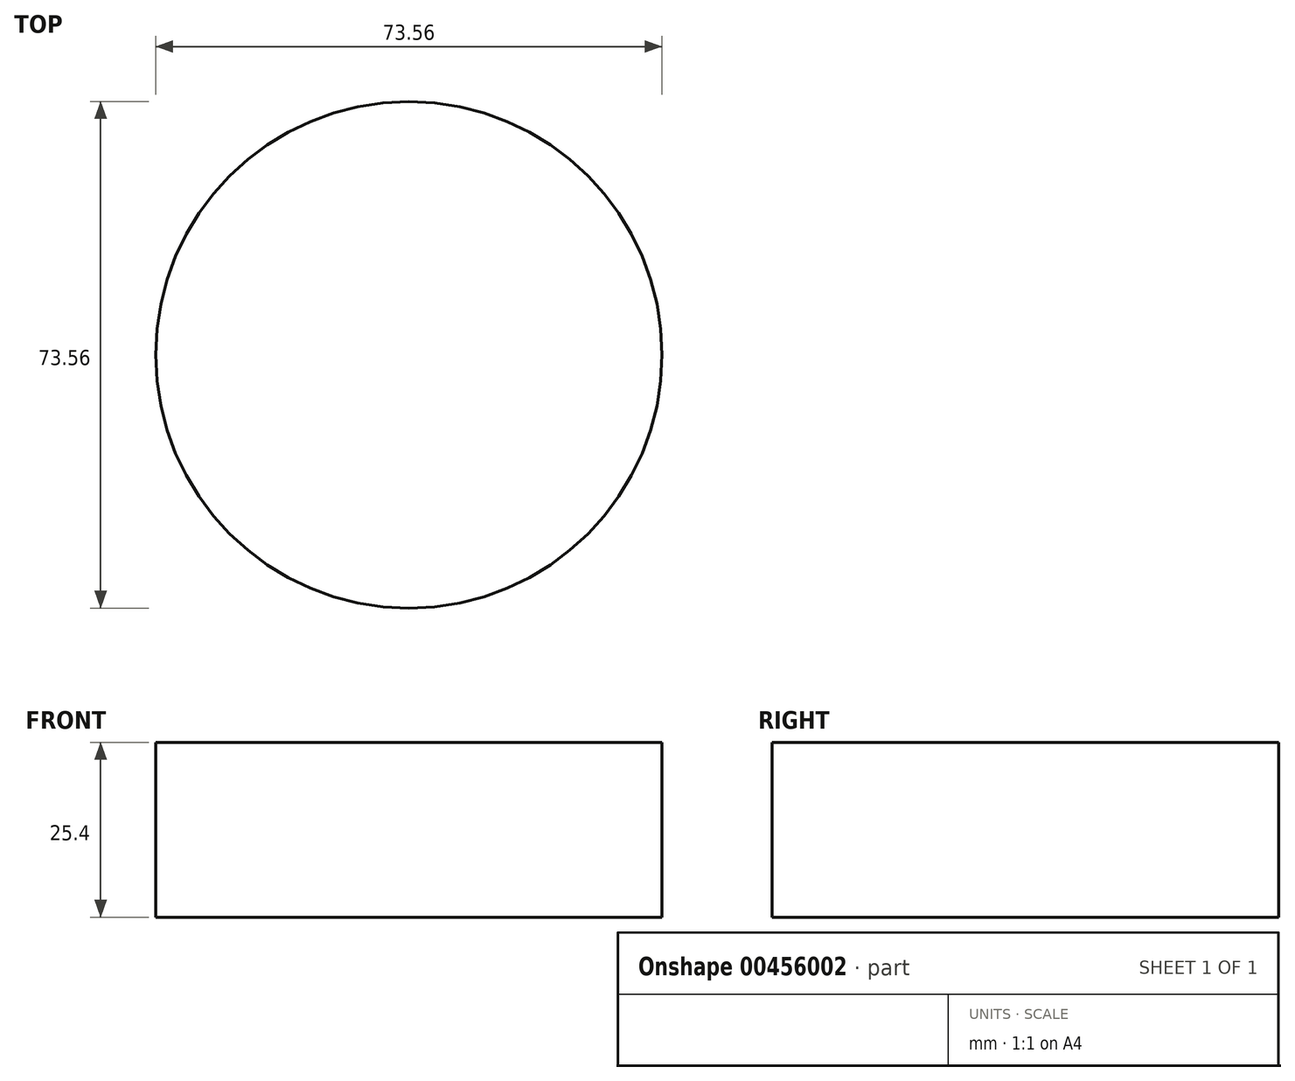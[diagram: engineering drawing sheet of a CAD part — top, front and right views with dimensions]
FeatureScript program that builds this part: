
annotation { "Feature Type Name" : "Feature", "Feature Type Description" : "" }
export const myFeature = defineFeature(function(context is Context, id is Id, definition is map)
    precondition{}
    {
        {
            var Q0;
            Q0=qCreatedBy(makeId("Top.planeOp"),FACE);
            var sketch = newSketch(context, id + "F0", { "sketchPlane" : qUnion([Q0])});
            skCircle(sketch, "E0", {"center": v(0, 0) * mm, "radius": 36.78 * mm});
            skSolve(sketch);
        }
        {
            var Q0;
            Q0 = qSketchRegion(id + "F0", true);
            extrude(context, id + "F1", {"entities" : qUnion([Q0]), "depth" : 25.4 * mm});
        }
    });
